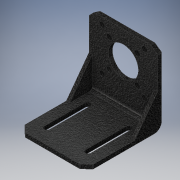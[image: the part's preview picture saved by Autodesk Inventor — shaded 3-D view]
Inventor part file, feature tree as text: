
AUTODESK INVENTOR PART (.ipt)
format: ipt  version: 2018 (Build 220112000, 112)  size: 248,832 bytes
history: native  units: in
note: dims shown in document units (in); Inventor stores cm internally (conversion verified against a paired STEP export)
features: sketch x8, extrude x6, plane x1, sweep x1, fillet x1, mirror x1
ambient origin geometry x8: Origin, YZ Plane, XZ Plane, XY Plane, X Axis, Y Axis, Z Axis, Center Point
bodies: Solid1 (feature_tree)
feature tree (18):
  sketch  "Sketch1"  dims[d0=1.0492in d1=1.0492in]
  plane  "Work Plane1"
  sweep  "Sweep1"
  extrude  "Extrusion1"  Depth=0.1575in
  extrude  "Extrusion2"  Depth=0.1181in
  extrude  "Extrusion3"  Depth=0.8661in
  extrude  "Extrusion4"  Depth=0.9843in
  extrude  "Extrusion5"  Depth=0.1575in
  fillet  "Fillet1"  Radius=0.6102in
  extrude  "Extrusion6"  Depth=0.1575in
  mirror  "Mirror1"
  sketch  "Sketch2"  dims[d2=2.0079in d3=0.1575in]
  sketch  "Sketch3"  dims[d4=1.9685in d5=0.1181in]
  sketch  "Sketch4"  dims[d6=0.0in d7=0.0in d8=0.8661in]
  sketch  "Sketch5"  dims[d9=0.8071in d10=0.9843in]
  sketch  "Sketch6"  dims[d11=0.3937in d12=0.0in d13=0.1575in d14=0.6102in]
  sketch  "Sketch7"  dims[d15=0.6102in d17=0.1575in]
  sketch  "Sketch8"  dims[d18=0.0591in d19=0.3937in d20=0.0in d21=0.7874in d22=0.7874in d23=0.3937in d24=0.0in d25=0.7874in d26=0.7874in d27=0.3937in d28=0.0in d29=1.3386in d30=0.1575in d31=0.315in d32=0.3543in d33=0.3937in d34=0.0in d35=0.0394in d36=1.1811in d37=0.9055in d38=0.0984in d39=0.0in]
